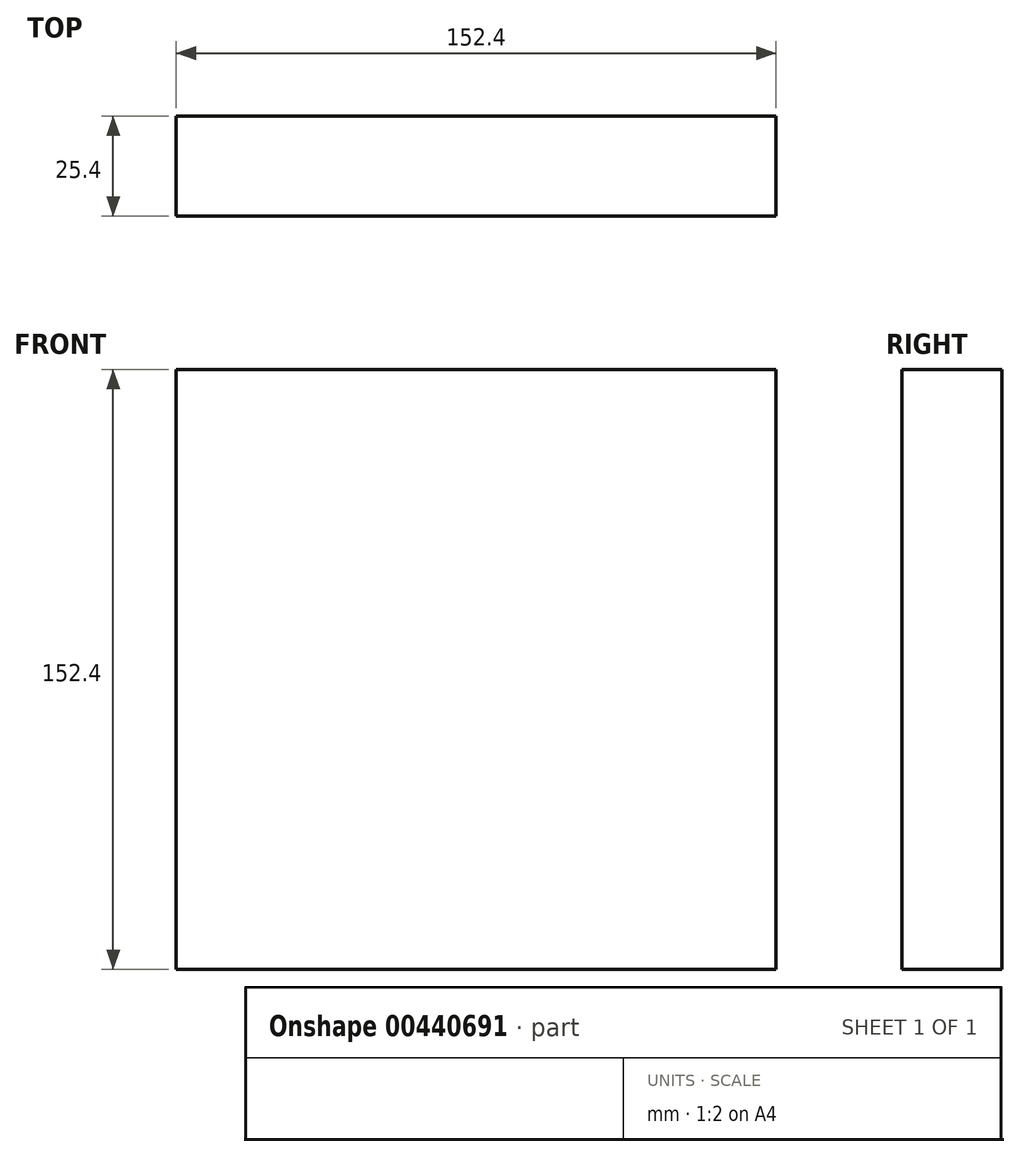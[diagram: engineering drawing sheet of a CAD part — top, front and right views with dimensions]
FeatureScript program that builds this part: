
annotation { "Feature Type Name" : "Feature", "Feature Type Description" : "" }
export const myFeature = defineFeature(function(context is Context, id is Id, definition is map)
    precondition{}
    {
        {
            var Q0;
            Q0=qCreatedBy(makeId("Front.planeOp"),FACE);
            var sketch = newSketch(context, id + "F0", { "sketchPlane" : qUnion([Q0])});
            skLineSegment(sketch, "E0.bottom", {"start": v(76.2, 68.58) * mm, "end": v(-76.2, 68.58) * mm});
            skLineSegment(sketch, "E0.top", {"start": v(76.2, -83.82) * mm, "end": v(-76.2, -83.82) * mm});
            skLineSegment(sketch, "E0.left", {"start": v(76.2, 68.58) * mm, "end": v(76.2, -83.82) * mm});
            skLineSegment(sketch, "E0.right", {"start": v(-76.2, 68.58) * mm, "end": v(-76.2, -83.82) * mm});
            skPoint(sketch, "E0.middle", {"position": v(0, -7.62) * mm});
            skSolve(sketch);
        }
        {
            var Q0;
            Q0=makeQuery(id+"F0.imprint","IMPRINT",FACE,{"disambiguationData":[TD([[makeQuery(id+"F0.imprint","IMPRINT",EDGE,{"derivedFrom":sQuery(id+"F0.wireOp",EDGE,"E0.bottom")}),1.0]])]});
            extrude(context, id + "F1", {"entities" : qUnion([Q0]), "depth" : 25.4 * mm});
        }
    });
